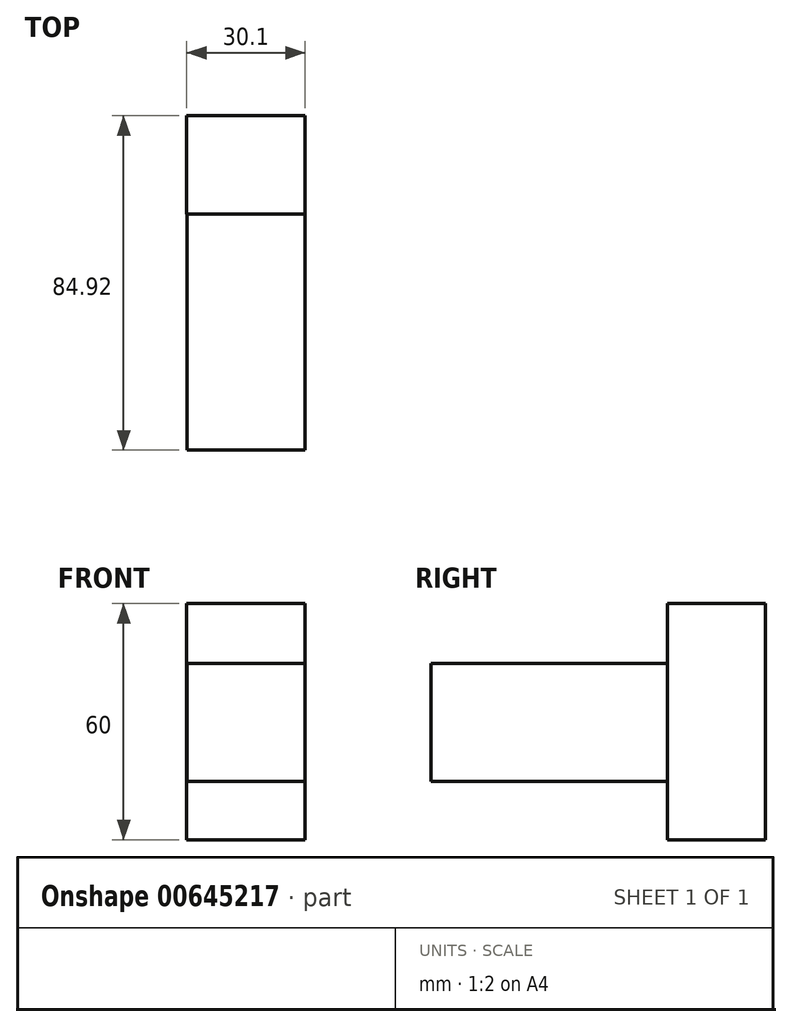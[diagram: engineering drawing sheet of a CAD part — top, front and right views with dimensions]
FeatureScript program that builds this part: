
annotation { "Feature Type Name" : "Feature", "Feature Type Description" : "" }
export const myFeature = defineFeature(function(context is Context, id is Id, definition is map)
    precondition{}
    {
        {
            var Q0;
            Q0=qCreatedBy(makeId("Front.planeOp"),FACE);
            var sketch = newSketch(context, id + "F0", { "sketchPlane" : qUnion([Q0])});
            skLineSegment(sketch, "E0.bottom", {"start": v(-31.9, 36.93) * mm, "end": v(-1.9, 36.93) * mm});
            skLineSegment(sketch, "E0.top", {"start": v(-31.9, -23.07) * mm, "end": v(-1.9, -23.07) * mm});
            skLineSegment(sketch, "E0.left", {"start": v(-31.9, 36.93) * mm, "end": v(-31.9, -23.07) * mm});
            skLineSegment(sketch, "E0.right", {"start": v(-1.9, 36.93) * mm, "end": v(-1.9, -23.07) * mm});
            skSolve(sketch);
        }
        {
            var Q0;
            Q0=makeQuery(id+"F0.imprint","IMPRINT",FACE,{"disambiguationData":[TD([[makeQuery(id+"F0.imprint","IMPRINT",EDGE,{"derivedFrom":sQuery(id+"F0.wireOp",EDGE,"E0.bottom")}),-1.0]])]});
            extrude(context, id + "F1", {"entities" : qUnion([Q0]), "depth" : 24.92 * mm, "offsetDistance" : 25.4 * mm});
        }
        {
            var Q0;
            Q0=makeQuery(id+"F1.opExtrude","CAP_FACE",FACE,{"disambiguationData":[OSD([sQuery(id+"F0.wireOp",EDGE,"E0.bottom"),sQuery(id+"F0.wireOp",EDGE,"E0.top"),sQuery(id+"F0.wireOp",EDGE,"E0.left"),sQuery(id+"F0.wireOp",EDGE,"E0.right")])],"isStart":false});
            var sketch = newSketch(context, id + "F2", { "sketchPlane" : qUnion([Q0])});
            skSolve(sketch);
        }
        {
            var Q0;
            Q0=makeQuery(id+"F2.imprint","IMPRINT",FACE,{"disambiguationData":[TD([[makeQuery(id+"F2.imprint","IMPRINT",EDGE,{"derivedFrom":makeQuery(id+"F1.opExtrude","CAP_EDGE",EDGE,{"disambiguationData":[OSD([sQuery(id+"F0.wireOp",EDGE,"E0.bottom")])],"isStart":false})}),-1.0]])]});
            var sketch = newSketch(context, id + "F3", { "sketchPlane" : qUnion([Q0])});
            skLineSegment(sketch, "E1.bottom", {"start": v(-31.79, 21.7) * mm, "end": v(-1.79, 21.7) * mm});
            skLineSegment(sketch, "E1.top", {"start": v(-31.79, -8.3) * mm, "end": v(-1.79, -8.3) * mm});
            skLineSegment(sketch, "E1.left", {"start": v(-31.79, 21.7) * mm, "end": v(-31.79, -8.3) * mm});
            skLineSegment(sketch, "E1.right", {"start": v(-1.79, 21.7) * mm, "end": v(-1.79, -8.3) * mm});
            skSolve(sketch);
        }
        {
            var Q0;
            Q0 = qSketchRegion(id + "F3", true);
            extrude(context, id + "F4", {"entities" : qUnion([Q0]), "operationType" : NewBodyOperationType.ADD, "depth" : 60 * mm, "offsetDistance" : 25.4 * mm});
        }
    });
